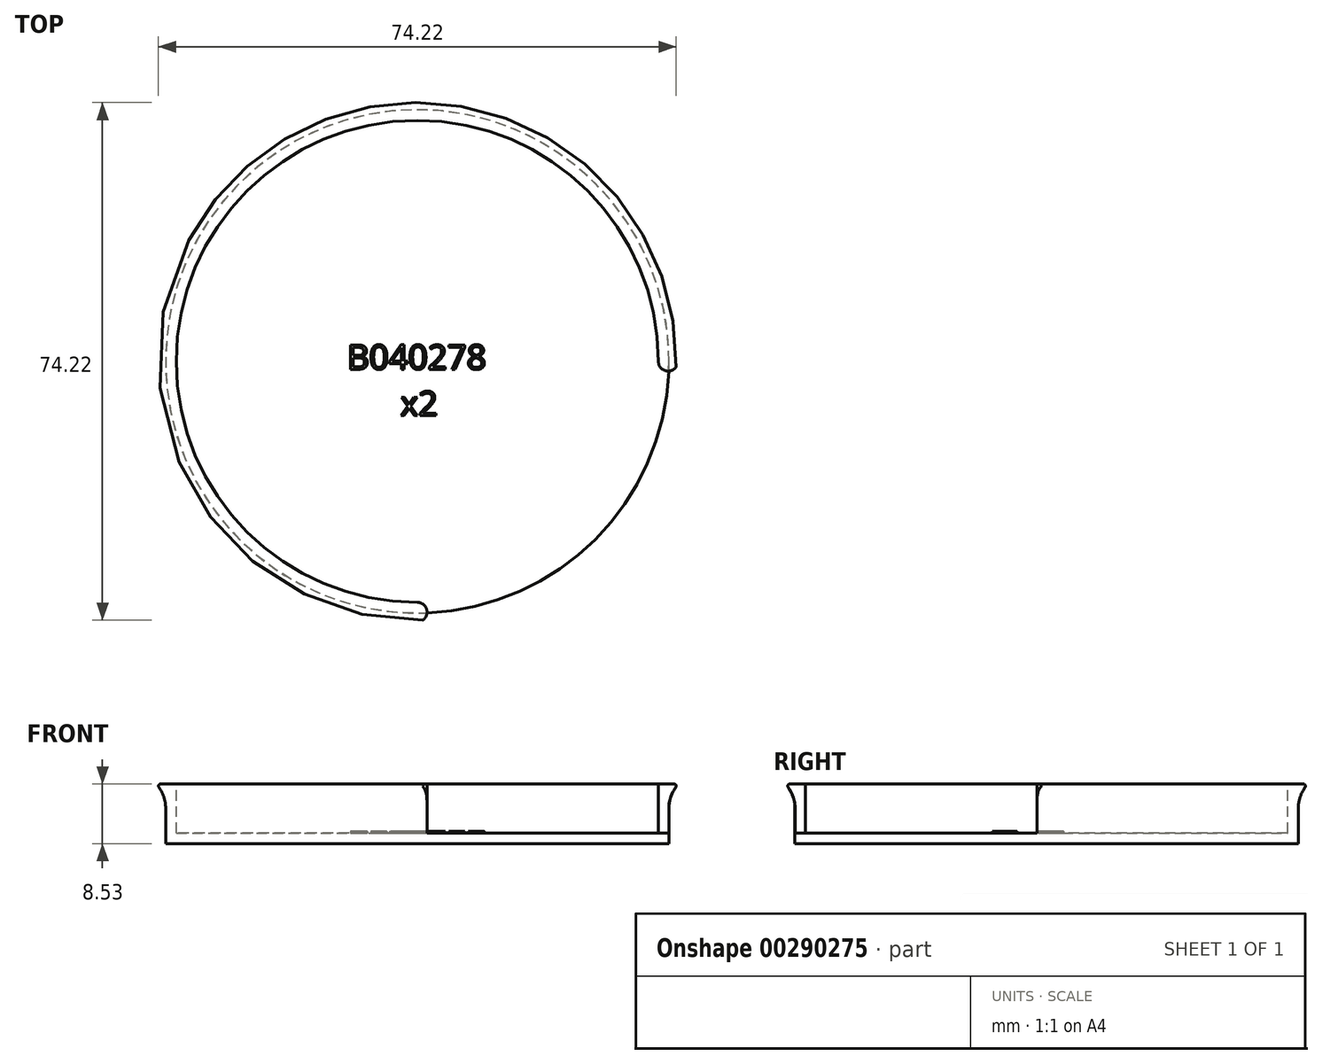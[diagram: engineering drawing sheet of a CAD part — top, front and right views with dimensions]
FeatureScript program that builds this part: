
annotation { "Feature Type Name" : "Feature", "Feature Type Description" : "" }
export const myFeature = defineFeature(function(context is Context, id is Id, definition is map)
    precondition{}
    {
        {
            var Q0;
            Q0=qCreatedBy(makeId("Right.planeOp"),FACE);
            var sketch = newSketch(context, id + "F0", { "sketchPlane" : qUnion([Q0])});
            skLineSegment(sketch, "E0", {"start": v(21.43, 8.53) * mm, "end": v(21.43, 0) * mm});
            skLineSegment(sketch, "E1", {"start": v(21.43, 8.53) * mm, "end": v(-15.93, 8.53) * mm});
            skLineSegment(sketch, "E2", {"start": v(21.43, 0) * mm, "end": v(-14.66, 0) * mm});
            skLineSegment(sketch, "E3", {"start": v(-14.66, 0) * mm, "end": v(-14.66, 6.5) * mm});
            skLineSegment(sketch, "E4", {"start": v(-14.66, 6.5) * mm, "end": v(-14.66, 8.53) * mm});
            skLineSegment(sketch, "E5", {"start": v(-15.93, 8.53) * mm, "end": v(-14.66, 6.5) * mm});
            skSolve(sketch);
        }
        {
            var Q0;
            Q0=qSketchRegion(id+"F0",true);
            var Q1;
            Q1=sQuery(id+"F0.wireOp",EDGE,"E0");
            revolve(context, id + "F1", {"entities" : qUnion([Q0]), "axis" : qUnion([Q1]), "revolveType" : RevolveType.FULL});
        }
        {
            var Q0;
            Q0=makeQuery(id+"F1.opRevolve","SWEPT_FACE",FACE,{"disambiguationData":[OSD([sQuery(id+"F0.wireOp",EDGE,"E1")])]});
            var sketch = newSketch(context, id + "F2", { "sketchPlane" : qUnion([Q0])});
            skArc(sketch, "E6", {"start": v(0, -15.93) * mm, "mid": v(1.4, -14.53) * mm, "end": v(0, -13.13) * mm});
            skCircle(sketch, "E7", {"center": v(0, 21.43) * mm, "radius": 34.56 * mm});
            skLineSegment(sketch, "E8", {"start": v(0, 21.43) * mm, "end": v(37.35, 21.43) * mm});
            skArc(sketch, "E9", {"start": v(34.56, 21.43) * mm, "mid": v(35.95, 20.03) * mm, "end": v(37.35, 21.43) * mm});
            skSolve(sketch);
        }
        {
            var Q0;
            {var subQ0=sQuery(id+"F2.wireOp",EDGE,"E6");Q0=makeQuery(id+"F2.imprint","IMPRINT",FACE,{"disambiguationData":[TD([[makeQuery(id+"F2.imprint","IMPRINT",EDGE,{"derivedFrom":subQ0}),-1.0]])]});}
            var Q1;
            {var subQ0=sQuery(id+"F2.wireOp",EDGE,"E7");var subQ1=makeQuery(id+"F2.imprint","INTERSECT",VERTEX,{"derivedFrom":[sQuery(id+"F2.wireOp",EDGE,"E6"),subQ0]});Q1=makeQuery(id+"F2.imprint","IMPRINT",FACE,{"disambiguationData":[TD([[makeQuery(id+"F2.imprint","IMPRINT",EDGE,{"disambiguationData":[TD([[subQ1,1.0]])],"derivedFrom":subQ0}),1.0]])]});}
            extrude(context, id + "F3", {"entities" : qUnion([Q0, Q1]), "operationType" : NewBodyOperationType.REMOVE, "oppositeDirection" : true, "depth" : 7 * mm});
        }
        {
            var Q0;
            Q0=makeQuery(id+"F1.opRevolve","SWEPT_EDGE",EDGE,{"disambiguationData":[OSD([sQuery(id+"F0.wireOp",EDGE,"E1"),sQuery(id+"F0.wireOp",EDGE,"E5")])]});
            var Q1;
            Q1=makeQuery(id+"F3.boolean.opBoolean","COPY",EDGE,{"derivedFrom":makeQuery(id+"F3.opExtrude","CAP_EDGE",EDGE,{"disambiguationData":[OSD([sQuery(id+"F2.wireOp",EDGE,"Hj940JX0-86ln-aeAX-7QBq-tXhmjeFzDDCG")])],"isStart":true})});
            fillet(context, id + "F4", {"entities" : qUnion([Q0, Q1]), "radius" : 0.3 * mm, "tangentPropagation" : true, "allowEdgeOverflow" : false});
        }
        {
            var Q0;
            Q0=makeQuery(id+"F1.opRevolve","SWEPT_EDGE",EDGE,{"disambiguationData":[OSD([sQuery(id+"F0.wireOp",EDGE,"E3"),sQuery(id+"F0.wireOp",EDGE,"E4"),sQuery(id+"F0.wireOp",EDGE,"E5")])]});
            fillet(context, id + "F5", {"entities" : qUnion([Q0]), "radius" : 5 * mm, "tangentPropagation" : true, "allowEdgeOverflow" : false});
        }
        {
            var Q0;
            Q0=makeQuery(id+"F3.boolean.opBoolean","COPY",FACE,{"derivedFrom":makeQuery(id+"F3.opExtrude","CAP_FACE",FACE,{"disambiguationData":[OSD([sQuery(id+"F0.wireOp",EDGE,"E1"),sQuery(id+"F0.wireOp",EDGE,"E5"),sQuery(id+"F2.wireOp",EDGE,"Hj940JX0-86ln-aeAX-7QBq-tXhmjeFzDDCG"),sQuery(id+"F2.wireOp",EDGE,"E6"),sQuery(id+"F2.wireOp",EDGE,"103zpbTG-KLVD-Bw5I-Qeg4-O77QYgVRE0Vj")])],"isStart":false})});
            var sketch = newSketch(context, id + "F6", { "sketchPlane" : qUnion([Q0])});
            skText(sketch, "E10", { "text": "B040278\n      x2", "fontName": "OpenSans-Regular.ttf"});
            const initialGuessF6  = {"E10": [-0.01006, 0.02029, 1, 0, 0.00352]};
            skSetInitialGuess(sketch, initialGuessF6);
            skSolve(sketch);
        }
        {
            var Q0;
            Q0=qSketchRegion(id+"F6",true);
            extrude(context, id + "F7", {"entities" : qUnion([Q0]), "operationType" : NewBodyOperationType.ADD, "depth" : 0.2 * mm});
        }
    });
